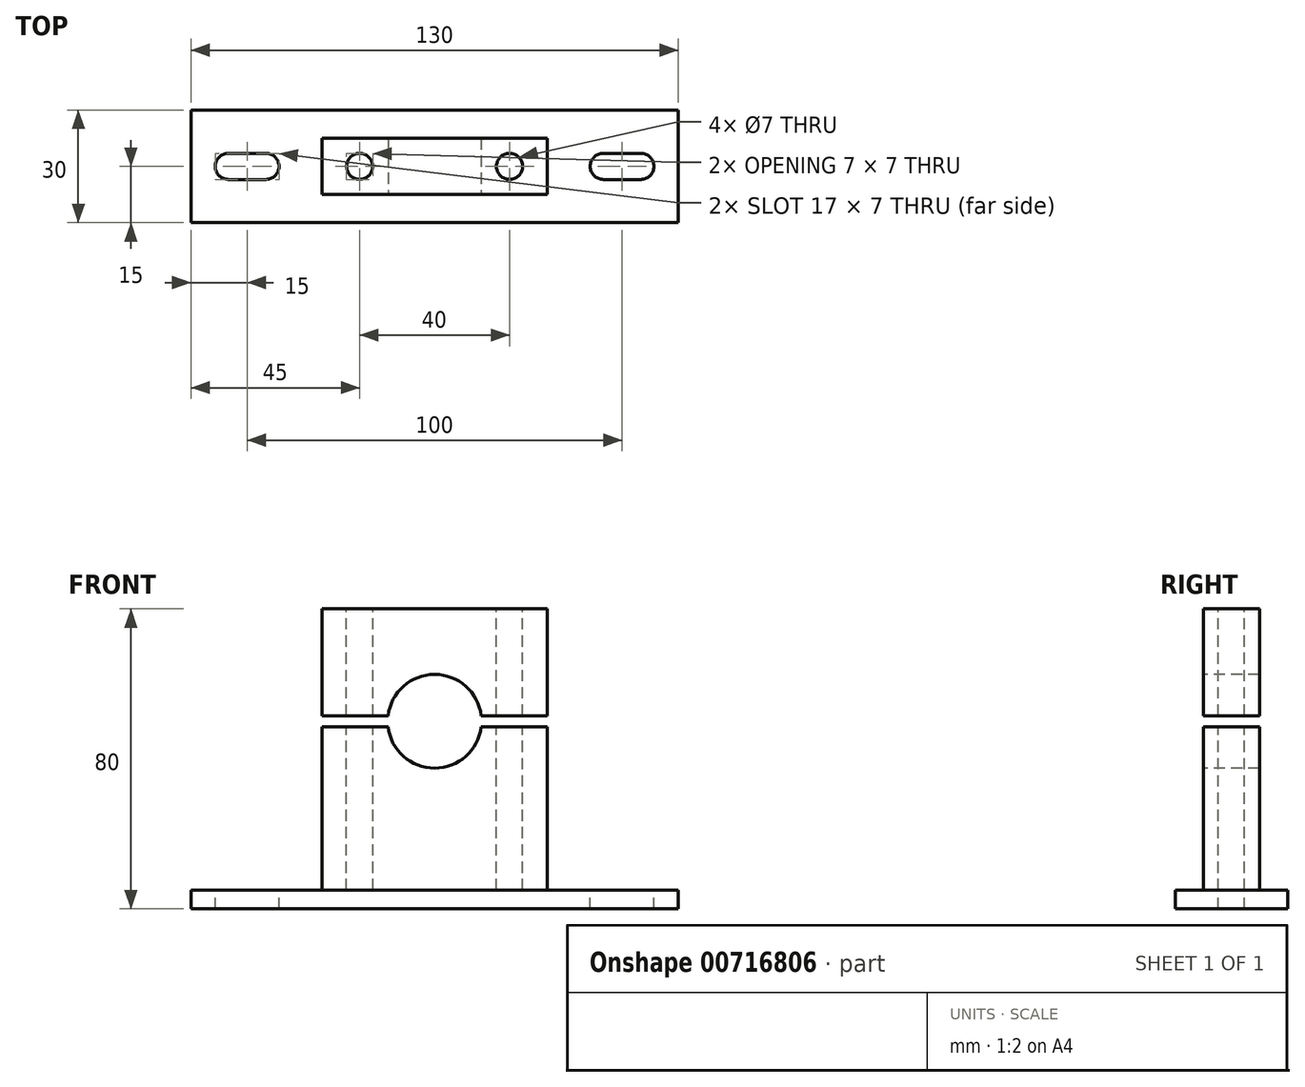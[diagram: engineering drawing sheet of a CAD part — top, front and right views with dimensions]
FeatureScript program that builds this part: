
annotation { "Feature Type Name" : "Feature", "Feature Type Description" : "" }
export const myFeature = defineFeature(function(context is Context, id is Id, definition is map)
    precondition{}
    {
        {
            var Q0;
            Q0=qCreatedBy(makeId("Top.planeOp"),FACE);
            var sketch = newSketch(context, id + "F0", { "sketchPlane" : qUnion([Q0])});
            skLineSegment(sketch, "E0.bottom", {"start": v(-65, 15) * mm, "end": v(65, 15) * mm});
            skLineSegment(sketch, "E0.top", {"start": v(-65, -15) * mm, "end": v(65, -15) * mm});
            skLineSegment(sketch, "E0.left", {"start": v(-65, 15) * mm, "end": v(-65, -15) * mm});
            skLineSegment(sketch, "E0.right", {"start": v(65, 15) * mm, "end": v(65, -15) * mm});
            skPoint(sketch, "E0.middle", {"position": v(0, 0) * mm});
            skSolve(sketch);
        }
        {
            var Q0;
            Q0 = qSketchRegion(id + "F0", true);
            extrude(context, id + "F1", {"entities" : qUnion([Q0]), "endBound" : BoundingType.SYMMETRIC, "depth" : 5 * mm, "offsetDistance" : 25 * mm});
        }
        {
            var Q0;
            Q0=makeQuery(id+"F1.opExtrude","CAP_FACE",FACE,{"disambiguationData":[OSD([sQuery(id+"F0.wireOp",EDGE,"E0.bottom"),sQuery(id+"F0.wireOp",EDGE,"E0.top"),sQuery(id+"F0.wireOp",EDGE,"E0.left"),sQuery(id+"F0.wireOp",EDGE,"E0.right")])],"isStart":false});
            var sketch = newSketch(context, id + "F2", { "sketchPlane" : qUnion([Q0])});
            skLineSegment(sketch, "E1.bottom", {"start": v(-30, 7.5) * mm, "end": v(30, 7.5) * mm});
            skLineSegment(sketch, "E1.top", {"start": v(-30, -7.5) * mm, "end": v(30, -7.5) * mm});
            skLineSegment(sketch, "E1.left", {"start": v(-30, 7.5) * mm, "end": v(-30, -7.5) * mm});
            skLineSegment(sketch, "E1.right", {"start": v(30, 7.5) * mm, "end": v(30, -7.5) * mm});
            skPoint(sketch, "E1.middle", {"position": v(0, 0) * mm});
            skSolve(sketch);
        }
        {
            var Q0;
            Q0 = qSketchRegion(id + "F2", true);
            extrude(context, id + "F3", {"entities" : qUnion([Q0]), "depth" : 75 * mm, "offsetDistance" : 25 * mm});
        }
        {
            var Q0;
            Q0=makeQuery(id+"F1.opExtrude","CAP_FACE",FACE,{"disambiguationData":[OSD([sQuery(id+"F0.wireOp",EDGE,"E0.bottom"),sQuery(id+"F0.wireOp",EDGE,"E0.top"),sQuery(id+"F0.wireOp",EDGE,"E0.left"),sQuery(id+"F0.wireOp",EDGE,"E0.right")])],"isStart":false});
            var sketch = newSketch(context, id + "F4", { "sketchPlane" : qUnion([Q0])});
            skCircle(sketch, "E2", {"center": v(55, 0) * mm, "radius": 3.5 * mm});
            skCircle(sketch, "E3", {"center": v(-55, 0) * mm, "radius": 3.5 * mm});
            skCircle(sketch, "E4", {"center": v(-45, 0) * mm, "radius": 3.5 * mm});
            skCircle(sketch, "E5", {"center": v(45, 0) * mm, "radius": 3.5 * mm});
            skLineSegment(sketch, "E6", {"start": v(-55, 3.5) * mm, "end": v(-45, 3.5) * mm});
            skLineSegment(sketch, "E7", {"start": v(-45, 3.5) * mm, "end": v(-45, -3.5) * mm});
            skLineSegment(sketch, "E8", {"start": v(-45, -3.5) * mm, "end": v(-55, -3.5) * mm});
            skLineSegment(sketch, "E9", {"start": v(45, 3.5) * mm, "end": v(55, 3.5) * mm});
            skLineSegment(sketch, "E10", {"start": v(55, 3.5) * mm, "end": v(55, -3.5) * mm});
            skLineSegment(sketch, "E11", {"start": v(55, -3.5) * mm, "end": v(45, -3.5) * mm});
            skSolve(sketch);
        }
        {
            var Q0;
            Q0 = qSketchRegion(id + "F4", true);
            extrude(context, id + "F5", {"entities" : qUnion([Q0]), "operationType" : NewBodyOperationType.REMOVE, "endBound" : BoundingType.THROUGH_ALL, "oppositeDirection" : true, "depth" : 25 * mm, "offsetDistance" : 25 * mm});
        }
        {
            var Q0;
            Q0=makeQuery(id+"F3.opExtrude","SWEPT_FACE",FACE,{"disambiguationData":[OSD([sQuery(id+"F2.wireOp",EDGE,"E1.top")])]});
            var sketch = newSketch(context, id + "F6", { "sketchPlane" : qUnion([Q0])});
            skCircle(sketch, "E12", {"center": v(0, 47.5) * mm, "radius": 12.5 * mm});
            skLineSegment(sketch, "E13.bottom", {"start": v(-30, 49) * mm, "end": v(30, 49) * mm});
            skLineSegment(sketch, "E13.top", {"start": v(-30, 46) * mm, "end": v(30, 46) * mm});
            skLineSegment(sketch, "E13.left", {"start": v(-30, 49) * mm, "end": v(-30, 46) * mm});
            skLineSegment(sketch, "E13.right", {"start": v(30, 49) * mm, "end": v(30, 46) * mm});
            skSolve(sketch);
        }
        {
            var Q0;
            Q0 = qSketchRegion(id + "F6", true);
            extrude(context, id + "F7", {"entities" : qUnion([Q0]), "operationType" : NewBodyOperationType.REMOVE, "endBound" : BoundingType.THROUGH_ALL, "oppositeDirection" : true, "depth" : 25 * mm, "offsetDistance" : 25 * mm});
        }
        {
            var Q0;
            Q0=makeQuery(id+"F3.opExtrude","CAP_FACE",FACE,{"disambiguationData":[OSD([sQuery(id+"F2.wireOp",EDGE,"E1.bottom"),sQuery(id+"F2.wireOp",EDGE,"E1.top"),sQuery(id+"F2.wireOp",EDGE,"E1.left"),sQuery(id+"F2.wireOp",EDGE,"E1.right")])],"isStart":false});
            var sketch = newSketch(context, id + "F8", { "sketchPlane" : qUnion([Q0])});
            skPoint(sketch, "E14", {"position": v(20, 0) * mm});
            skPoint(sketch, "E15", {"position": v(-20, 0) * mm});
            skSolve(sketch);
        }
        {
            var Q0;
            Q0=sQuery(id+"F8.wireOp",VERTEX,"E15");
            var Q1;
            Q1=sQuery(id+"F8.wireOp",VERTEX,"E14");
            var Q2;
            Q2=makeQuery(id+"F7.boolean.opBoolean","SPLIT",BODY,{"disambiguationData":[OD(1.0)],"derivedFrom":makeQuery(id+"F3.opExtrude","SWEPT_BODY",BODY,{"disambiguationData":[OSD([sQuery(id+"F2.wireOp",EDGE,"E1.bottom"),sQuery(id+"F2.wireOp",EDGE,"E1.top"),sQuery(id+"F2.wireOp",EDGE,"E1.left"),sQuery(id+"F2.wireOp",EDGE,"E1.right")])]})});
            hole(context, id + "F9", {"style" : HoleStyle.SIMPLE, "endStyle" : HoleEndStyle.THROUGH, "standardTappedOrClearance" : lookupTablePath({ "standard" : "ISO", "size" : "7", "type" : "Drilled" }), "standardBlindInLast" : lookupTablePath({ "standard" : "ISO", "size" : "7", "type" : "Drilled" }), "holeDiameter" : 7 * mm, "majorDiameter" : 6 * mm, "isTappedThrough" : true, "tappedDepth" : 15 * mm, "tapClearance" : 3, "startFromSketch" : true, "locations" : qUnion([Q0, Q1]), "scope" : qUnion([Q2])});
        }
        {
            var Q0;
            {var subQ0=sQuery(id+"F6.wireOp",EDGE,"E13.top");Q0=makeQuery(id+"F7.boolean.opBoolean","COPY",FACE,{"derivedFrom":makeQuery(id+"F7.opExtrude","SWEPT_FACE",FACE,{"disambiguationData":[OSD([subQ0]),TDD([makeQuery(id+"F6.imprint","IMPRINT",EDGE,{"disambiguationData":[TD([[makeQuery(id+"F6.imprint","INTERSECT",VERTEX,{"disambiguationData":[OD(1.0)],"derivedFrom":[sQuery(id+"F6.wireOp",EDGE,"E12"),subQ0]}),-1.0]])],"derivedFrom":subQ0})])]})});}
            var sketch = newSketch(context, id + "F10", { "sketchPlane" : qUnion([Q0])});
            skPoint(sketch, "E16", {"position": v(20, 0) * mm});
            skPoint(sketch, "E17", {"position": v(-20, 0) * mm});
            skSolve(sketch);
        }
        {
            var Q0;
            Q0=sQuery(id+"F10.wireOp",VERTEX,"E16");
            var Q1;
            Q1=sQuery(id+"F10.wireOp",VERTEX,"E17");
            var Q2;
            Q2=makeQuery(id+"F7.boolean.opBoolean","SPLIT",BODY,{"disambiguationData":[OD(0.0)],"derivedFrom":makeQuery(id+"F3.opExtrude","SWEPT_BODY",BODY,{"disambiguationData":[OSD([sQuery(id+"F2.wireOp",EDGE,"E1.bottom"),sQuery(id+"F2.wireOp",EDGE,"E1.top"),sQuery(id+"F2.wireOp",EDGE,"E1.left"),sQuery(id+"F2.wireOp",EDGE,"E1.right")])]})});
            hole(context, id + "F11", {"style" : HoleStyle.SIMPLE, "endStyle" : HoleEndStyle.BLIND, "standardTappedOrClearance" : lookupTablePath({ "standard" : "ISO", "engagement" : "75%", "pitch" : "1 mm", "size" : "M6", "type" : "Tapped" }), "standardBlindInLast" : lookupTablePath({ "standard" : "ISO", "engagement" : "75%", "pitch" : "1 mm", "size" : "M6", "type" : "Tapped" }), "holeDiameter" : 5 * mm, "majorDiameter" : 6 * mm, "showTappedDepth" : true, "holeDepth" : 18 * mm, "isTappedThrough" : true, "tappedDepth" : 15 * mm, "tapClearance" : 3, "startFromSketch" : true, "locations" : qUnion([Q0, Q1]), "scope" : qUnion([Q2])});
        }
    });
